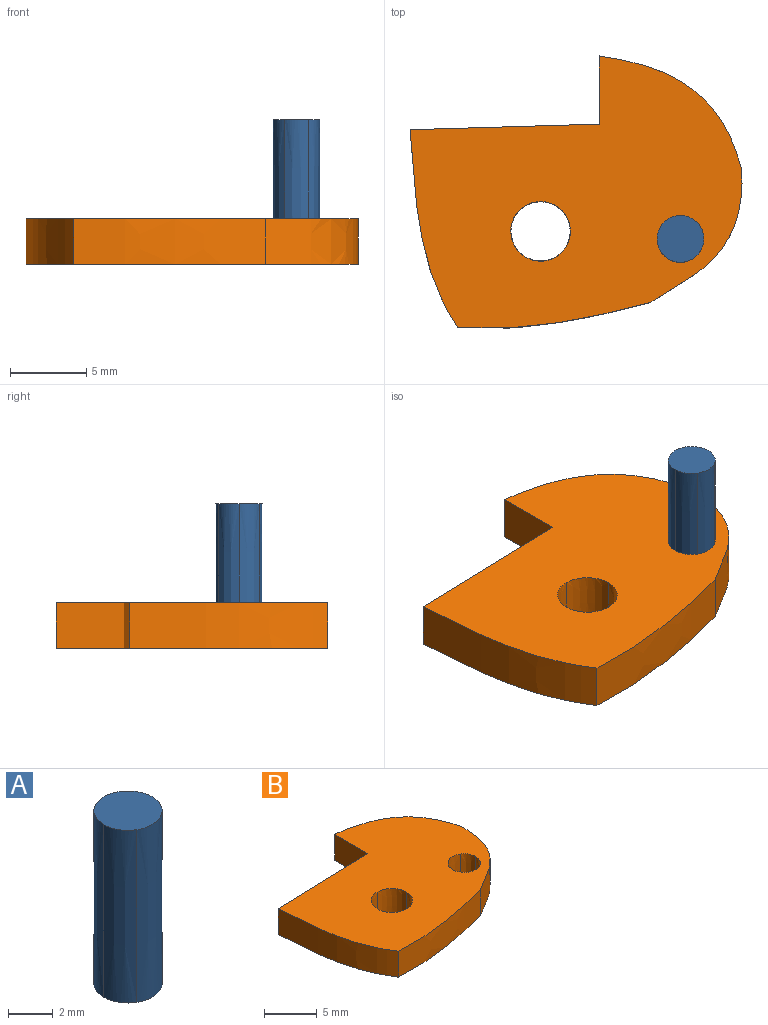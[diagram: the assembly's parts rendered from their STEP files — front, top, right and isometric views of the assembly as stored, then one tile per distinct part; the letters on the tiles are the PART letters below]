
ASSEMBLY  parts=2 mates=1
PART A: 8 faces, bbox 3.1x3.1x9.5 mm
  f0: extruded ~9.5x1.33mm, area 15.3mm2, adj f1,f5,f6,f7
  f1: extruded ~9.5x1.33mm, area 15.3mm2, adj f0,f2,f6,f7
  f2: extruded ~9.5x1.53mm, area 15.3mm2, adj f1,f3,f6,f7
  f3: extruded ~9.5x1.33mm, area 15.3mm2, adj f2,f4,f6,f7
  f4: extruded ~9.5x1.33mm, area 15.3mm2, adj f3,f5,f6,f7
  f5: extruded ~9.5x1.53mm, area 15.3mm2, adj f0,f4,f6,f7
  f6: plane 3.14x3.07mm, normal (0,0,1), area 7.4mm2, adj f0,f1,f2,f3,f4,f5
  f7: plane 3.14x3.07mm, normal (0,0,-1), area 7.4mm2, adj f0,f1,f2,f3,f4,f5
PART B: 19 faces, bbox 22.1x18x3 mm
  f0: extruded ~9.36x7.45mm, area 38.6mm2, adj f1,f16,f17,f18
  f1: plane 4.47x3mm, normal (-1,0,0), area 13.4mm2, adj f0,f2,f17,f18
  f2: plane 12.39x3mm, normal (-0.03,1,0), area 37.2mm2, adj f1,f3,f17,f18
  f3: extruded ~12.99x3.13mm, area 40.6mm2, adj f2,f4,f17,f18
  f4: extruded ~12.6x3mm, area 38.3mm2, adj f3,f16,f17,f18
  f5: extruded ~3x1.96mm, area 9.2mm2, adj f6,f14,f17,f18
  f6: extruded ~3x1.69mm, area 6.1mm2, adj f5,f7,f17,f18
  f7: extruded ~3x1.96mm, area 6.1mm2, adj f6,f8,f17,f18
  f8: extruded ~3x1.69mm, area 6.1mm2, adj f7,f14,f17,f18
  f9: extruded ~3x1.33mm, area 4.8mm2, adj f10,f15,f17,f18
  f10: extruded ~3x1.33mm, area 4.8mm2, adj f9,f11,f17,f18
  f11: extruded ~3x1.53mm, area 4.8mm2, adj f10,f12,f17,f18
  f12: extruded ~3x1.33mm, area 4.8mm2, adj f11,f13,f17,f18
  f13: extruded ~3x1.33mm, area 4.8mm2, adj f12,f15,f17,f18
  f14: extruded ~3x1.96mm, area 9.2mm2, adj f5,f8,f17,f18
  f15: extruded ~3x1.53mm, area 4.8mm2, adj f9,f13,f17,f18
  f16: extruded ~8.72x6.04mm, area 34.2mm2, adj f0,f4,f17,f18
  f17: plane 22.05x18.01mm, normal (0,0,1), area 250.6mm2, adj f0,f1,f2,f3,f4,f5,f6,f7
  f18: plane 22.05x18.01mm, normal (0,0,-1), area 250.6mm2, adj f0,f1,f2,f3,f4,f5,f6,f7
PLACE A at identity
PLACE B t=(-6.85,3.06,0)mm
MATE fastened B.f18 <-> A.f7  axis (0,0,-1) through (0,0,0)mm
